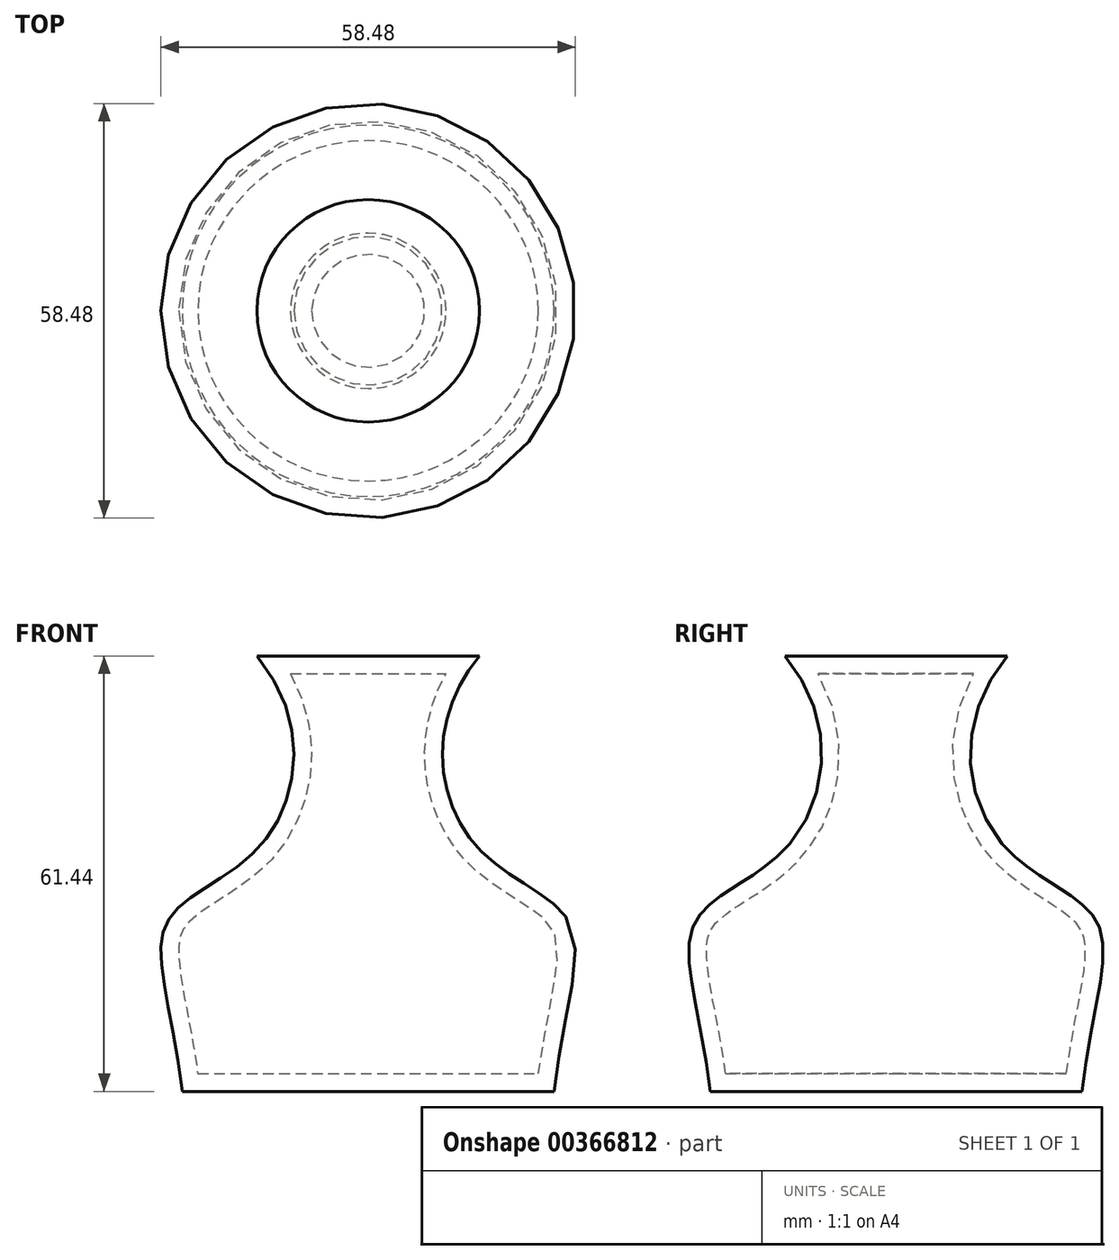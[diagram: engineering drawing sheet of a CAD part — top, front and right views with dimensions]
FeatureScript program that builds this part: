
annotation { "Feature Type Name" : "Feature", "Feature Type Description" : "" }
export const myFeature = defineFeature(function(context is Context, id is Id, definition is map)
    precondition{}
    {
        {
            var Q0;
            Q0=qCreatedBy(makeId("Front.planeOp"),FACE);
            var sketch = newSketch(context, id + "F0", { "sketchPlane" : qUnion([Q0])});
            skLineSegment(sketch, "E0", {"start": v(0, 0) * mm, "end": v(0, 61.44) * mm});
            skLineSegment(sketch, "E1", {"start": v(0, 61.44) * mm, "end": v(-15.7, 61.44) * mm});
            skFitSpline(sketch, "E2", {"points": [v(-15.7, 61.44) * mm, v(-15.07, 34.85) * mm, v(-28.14, 24.3) * mm, v(-26.22, 0) * mm], "startDerivative": vector(63.8, -77.18) * mm, "endDerivative": vector(12.68, -107.21) * mm});
            skLineSegment(sketch, "E3", {"start": v(-26.22, 0) * mm, "end": v(0, 0) * mm});
            skSolve(sketch);
        }
        {
            var Q0;
            Q0=makeQuery(id+"F0.imprint","IMPRINT",FACE,{"disambiguationData":[TD([[makeQuery(id+"F0.imprint","IMPRINT",EDGE,{"derivedFrom":sQuery(id+"F0.wireOp",EDGE,"E0")}),1.0]])]});
            var Q1;
            Q1=sQuery(id+"F0.wireOp",EDGE,"E0");
            revolve(context, id + "F1", {"entities" : qUnion([Q0]), "axis" : qUnion([Q1]), "revolveType" : RevolveType.FULL});
        }
        {
            var Q0;
            Q0=makeQuery(id+"F1.opRevolve","SWEPT_FACE",FACE,{"disambiguationData":[OSD([sQuery(id+"F0.wireOp",EDGE,"E2")])]});
            var Q1;
            Q1=makeQuery(id+"F1.opRevolve","SWEPT_FACE",FACE,{"disambiguationData":[OSD([sQuery(id+"F0.wireOp",EDGE,"E1")])]});
            var Q2;
            Q2=makeQuery(id+"F1.opRevolve","SWEPT_BODY",BODY,{"disambiguationData":[OSD([sQuery(id+"F0.wireOp",EDGE,"E0"),sQuery(id+"F0.wireOp",EDGE,"E1"),sQuery(id+"F0.wireOp",EDGE,"E2"),sQuery(id+"F0.wireOp",EDGE,"E3")])]});
            shell(context, id + "F2", {"isHollow" : true, "entities" : qUnion([Q0, Q1]), "parts" : qUnion([Q2]), "thickness" : 2.5 * mm});
        }
    });
